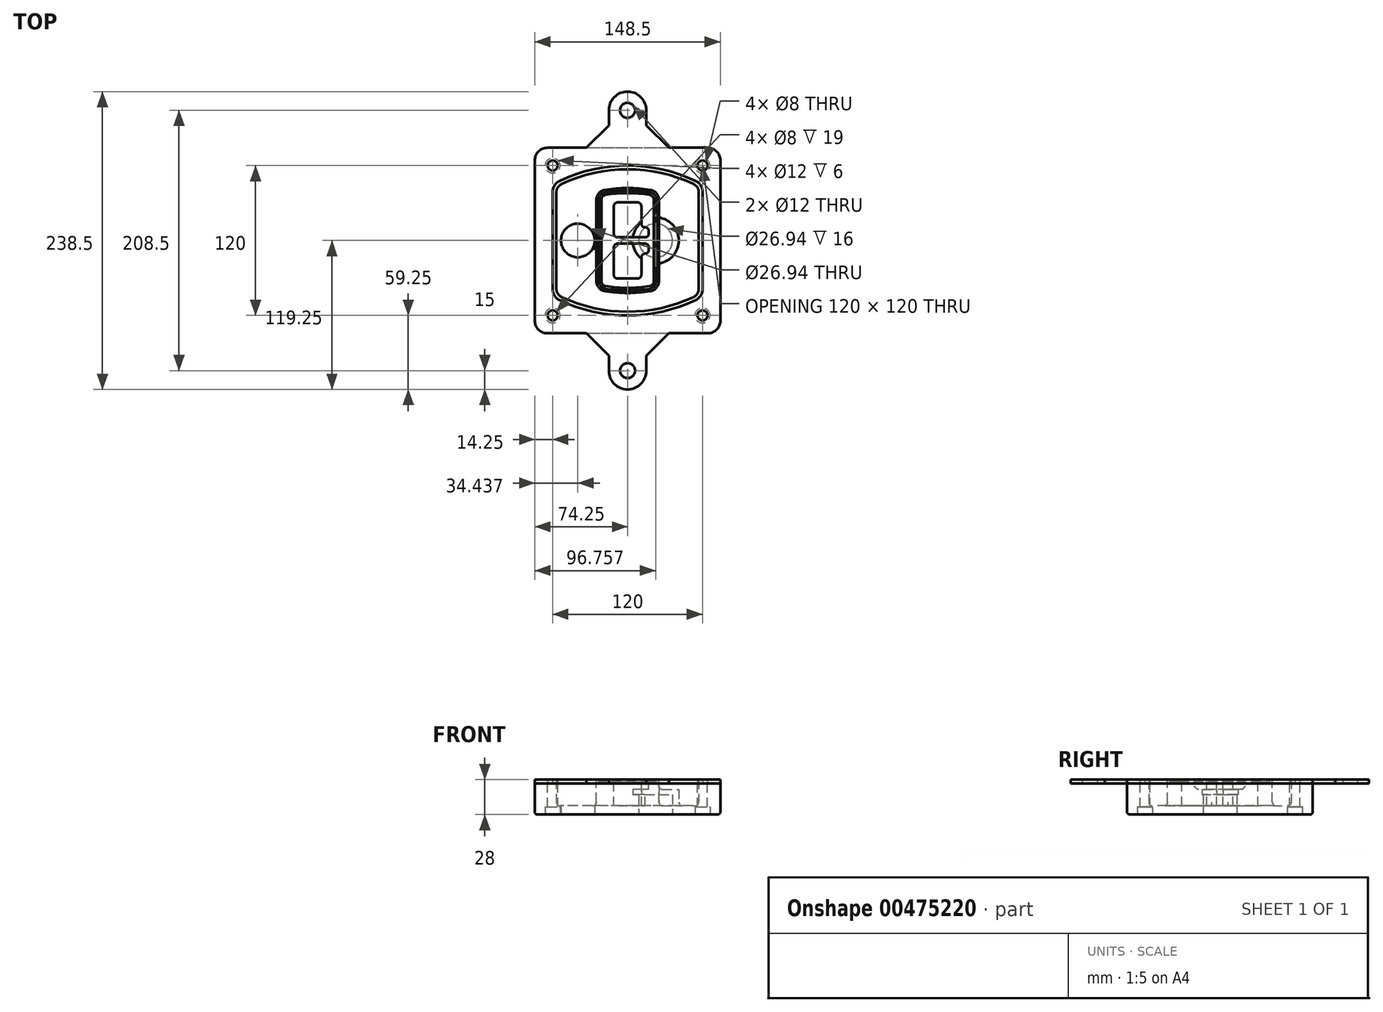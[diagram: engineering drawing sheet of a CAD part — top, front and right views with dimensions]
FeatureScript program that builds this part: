
annotation { "Feature Type Name" : "Feature", "Feature Type Description" : "" }
export const myFeature = defineFeature(function(context is Context, id is Id, definition is map)
    precondition{}
    {
        {
            var Q0;
            Q0=qCreatedBy(makeId("Top.planeOp"),FACE);
            var sketch = newSketch(context, id + "F0", { "sketchPlane" : qUnion([Q0])});
            skPoint(sketch, "E0.rect.middle", {"position": v(0, 0) * mm});
            skLineSegment(sketch, "E1.bottom", {"start": v(-64.25, -74.25) * mm, "end": v(64.25, -74.25) * mm});
            skLineSegment(sketch, "E1.top", {"start": v(-64.25, 74.25) * mm, "end": v(64.25, 74.25) * mm});
            skLineSegment(sketch, "E1.left", {"start": v(-74.25, -64.25) * mm, "end": v(-74.25, 64.25) * mm});
            skLineSegment(sketch, "E1.right", {"start": v(74.25, -64.25) * mm, "end": v(74.25, 64.25) * mm});
            skLineSegment(sketch, "E2", {"start": v(-74.25, 74.25) * mm, "end": v(74.25, -74.25) * mm, "construction": true});
            skLineSegment(sketch, "E3", {"start": v(74.25, 74.25) * mm, "end": v(-74.25, -74.25) * mm, "construction": true});
            skCircle(sketch, "E4", {"center": v(-60, 60) * mm, "radius": 4 * mm});
            skCircle(sketch, "E5", {"center": v(60, 60) * mm, "radius": 4 * mm});
            skCircle(sketch, "E6", {"center": v(60, -60) * mm, "radius": 4 * mm});
            skCircle(sketch, "E7", {"center": v(-60, -60) * mm, "radius": 4 * mm});
            skLineSegment(sketch, "E8", {"start": v(-60, 60) * mm, "end": v(60, 60) * mm, "construction": true});
            skLineSegment(sketch, "E9", {"start": v(60, 60) * mm, "end": v(60, -60) * mm, "construction": true});
            skLineSegment(sketch, "E10", {"start": v(60, -60) * mm, "end": v(-60, -60) * mm, "construction": true});
            skLineSegment(sketch, "E11", {"start": v(-60, -60) * mm, "end": v(-60, 60) * mm, "construction": true});
            skLineSegment(sketch, "E12", {"start": v(-60, 38.83) * mm, "end": v(-60, -38.83) * mm});
            skLineSegment(sketch, "E13", {"start": v(60, 38.83) * mm, "end": v(60, -38.83) * mm});
            skArc(sketch, "E14", {"start": v(54.26, 47.88) * mm, "mid": v(0, 60) * mm, "end": v(-54.26, 47.88) * mm});
            skArc(sketch, "E15", {"start": v(-54.26, -47.88) * mm, "mid": v(0, -60) * mm, "end": v(54.26, -47.88) * mm});
            skLineSegment(sketch, "E16", {"start": v(-60, 0) * mm, "end": v(60, 0) * mm, "construction": true});
            skPoint(sketch, "E17.visualSharp", {"position": v(-60, -45) * mm});
            skArc(sketch, "E17.filletArc", {"start": v(-60, -38.83) * mm, "mid": v(-58.44, -44.2) * mm, "end": v(-54.26, -47.88) * mm});
            skPoint(sketch, "E18.visualSharp", {"position": v(-60, 45) * mm});
            skArc(sketch, "E18.filletArc", {"start": v(-54.26, 47.88) * mm, "mid": v(-58.44, 44.2) * mm, "end": v(-60, 38.83) * mm});
            skPoint(sketch, "E19.visualSharp", {"position": v(60, 45) * mm});
            skArc(sketch, "E19.filletArc", {"start": v(60, 38.83) * mm, "mid": v(58.44, 44.2) * mm, "end": v(54.26, 47.88) * mm});
            skPoint(sketch, "E20.visualSharp", {"position": v(60, -45) * mm});
            skArc(sketch, "E20.filletArc", {"start": v(54.26, -47.88) * mm, "mid": v(58.44, -44.2) * mm, "end": v(60, -38.83) * mm});
            skPoint(sketch, "E21.visualSharp", {"position": v(-74.25, 74.25) * mm});
            skArc(sketch, "E21.filletArc", {"start": v(-64.25, 74.25) * mm, "mid": v(-71.32, 71.32) * mm, "end": v(-74.25, 64.25) * mm});
            skPoint(sketch, "E22.visualSharp", {"position": v(74.25, 74.25) * mm});
            skArc(sketch, "E22.filletArc", {"start": v(74.25, 64.25) * mm, "mid": v(71.32, 71.32) * mm, "end": v(64.25, 74.25) * mm});
            skPoint(sketch, "E23.visualSharp", {"position": v(74.25, -74.25) * mm});
            skArc(sketch, "E23.filletArc", {"start": v(64.25, -74.25) * mm, "mid": v(71.32, -71.32) * mm, "end": v(74.25, -64.25) * mm});
            skPoint(sketch, "E24.visualSharp", {"position": v(-74.25, -74.25) * mm});
            skArc(sketch, "E24.filletArc", {"start": v(-74.25, -64.25) * mm, "mid": v(-71.32, -71.32) * mm, "end": v(-64.25, -74.25) * mm});
            skArc(sketch, "E25.0", {"start": v(57, 38.83) * mm, "mid": v(55.9, 42.58) * mm, "end": v(52.98, 45.17) * mm});
            skLineSegment(sketch, "E25.1", {"start": v(57, 38.83) * mm, "end": v(57, -38.83) * mm});
            skArc(sketch, "E25.2", {"start": v(52.98, -45.17) * mm, "mid": v(55.9, -42.58) * mm, "end": v(57, -38.83) * mm});
            skArc(sketch, "E25.3", {"start": v(-52.98, -45.17) * mm, "mid": v(0, -57) * mm, "end": v(52.98, -45.17) * mm});
            skArc(sketch, "E25.4", {"start": v(-57, -38.83) * mm, "mid": v(-55.9, -42.58) * mm, "end": v(-52.98, -45.17) * mm});
            skArc(sketch, "E25.5", {"start": v(52.98, 45.17) * mm, "mid": v(0, 57) * mm, "end": v(-52.98, 45.17) * mm});
            skLineSegment(sketch, "E25.6", {"start": v(-57, 38.83) * mm, "end": v(-57, -38.83) * mm});
            skArc(sketch, "E25.7", {"start": v(-52.98, 45.17) * mm, "mid": v(-55.9, 42.58) * mm, "end": v(-57, 38.83) * mm});
            skArc(sketch, "E26.0", {"start": v(-55.96, 51.5) * mm, "mid": v(-61.82, 46.33) * mm, "end": v(-64, 38.83) * mm});
            skArc(sketch, "E26.1", {"start": v(55.96, 51.5) * mm, "mid": v(0, 64) * mm, "end": v(-55.96, 51.5) * mm});
            skArc(sketch, "E26.2", {"start": v(64, 38.83) * mm, "mid": v(61.82, 46.33) * mm, "end": v(55.96, 51.5) * mm});
            skLineSegment(sketch, "E26.3", {"start": v(64, 38.83) * mm, "end": v(64, -38.83) * mm});
            skArc(sketch, "E26.4", {"start": v(55.96, -51.5) * mm, "mid": v(61.82, -46.33) * mm, "end": v(64, -38.83) * mm});
            skLineSegment(sketch, "E26.5", {"start": v(-64, 38.83) * mm, "end": v(-64, -38.83) * mm});
            skArc(sketch, "E26.6", {"start": v(-55.96, -51.5) * mm, "mid": v(0, -64) * mm, "end": v(55.96, -51.5) * mm});
            skArc(sketch, "E26.7", {"start": v(-64, -38.83) * mm, "mid": v(-61.82, -46.33) * mm, "end": v(-55.96, -51.5) * mm});
            skSolve(sketch);
        }
        {
            var Q0;
            Q0=makeQuery(id+"F0.imprint","IMPRINT",FACE,{"disambiguationData":[TD([[makeQuery(id+"F0.imprint","IMPRINT",EDGE,{"derivedFrom":sQuery(id+"F0.wireOp",EDGE,"E1.bottom")}),1.0]])]});
            var Q1;
            Q1=makeQuery(id+"F0.imprint","IMPRINT",FACE,{"disambiguationData":[TD([[makeQuery(id+"F0.imprint","IMPRINT",EDGE,{"derivedFrom":sQuery(id+"F0.wireOp",EDGE,"E12")}),1.0]])]});
            var Q2;
            Q2=makeQuery(id+"F0.imprint","IMPRINT",FACE,{"disambiguationData":[TD([[makeQuery(id+"F0.imprint","IMPRINT",EDGE,{"derivedFrom":sQuery(id+"F0.wireOp",EDGE,"E25.0")}),1.0]])]});
            var Q3;
            Q3=makeQuery(id+"F0.imprint","IMPRINT",FACE,{"disambiguationData":[TD([[makeQuery(id+"F0.imprint","IMPRINT",EDGE,{"derivedFrom":sQuery(id+"F0.wireOp",EDGE,"E12")}),-1.0]])]});
            extrude(context, id + "F1", {"entities" : qUnion([Q0, Q1, Q2, Q3]), "oppositeDirection" : true, "depth" : 25 * mm});
        }
        {
            var Q0;
            Q0=makeQuery(id+"F0.imprint","IMPRINT",FACE,{"disambiguationData":[TD([[makeQuery(id+"F0.imprint","IMPRINT",EDGE,{"derivedFrom":sQuery(id+"F0.wireOp",EDGE,"E12")}),1.0]])]});
            extrude(context, id + "F2", {"entities" : qUnion([Q0]), "operationType" : NewBodyOperationType.ADD, "depth" : 3 * mm});
        }
        {
            var Q0;
            Q0=makeQuery(id+"F0.imprint","IMPRINT",FACE,{"disambiguationData":[TD([[makeQuery(id+"F0.imprint","IMPRINT",EDGE,{"derivedFrom":sQuery(id+"F0.wireOp",EDGE,"E25.0")}),1.0]])]});
            extrude(context, id + "F3", {"entities" : qUnion([Q0]), "operationType" : NewBodyOperationType.REMOVE, "oppositeDirection" : true, "depth" : 18 * mm});
        }
        {
            var Q0;
            Q0=makeQuery(id+"F2.opExtrude","CAP_FACE",FACE,{"disambiguationData":[OSD([sQuery(id+"F0.wireOp",EDGE,"E12"),sQuery(id+"F0.wireOp",EDGE,"E13"),sQuery(id+"F0.wireOp",EDGE,"E14"),sQuery(id+"F0.wireOp",EDGE,"E15"),sQuery(id+"F0.wireOp",EDGE,"E17.filletArc"),sQuery(id+"F0.wireOp",EDGE,"E18.filletArc"),sQuery(id+"F0.wireOp",EDGE,"E19.filletArc"),sQuery(id+"F0.wireOp",EDGE,"E20.filletArc"),sQuery(id+"F0.wireOp",EDGE,"E25.0"),sQuery(id+"F0.wireOp",EDGE,"E25.1"),sQuery(id+"F0.wireOp",EDGE,"E25.2"),sQuery(id+"F0.wireOp",EDGE,"E25.3"),sQuery(id+"F0.wireOp",EDGE,"E25.4"),sQuery(id+"F0.wireOp",EDGE,"E25.5"),sQuery(id+"F0.wireOp",EDGE,"E25.6"),sQuery(id+"F0.wireOp",EDGE,"E25.7")])],"isStart":false});
            var sketch = newSketch(context, id + "F4", { "sketchPlane" : qUnion([Q0])});
            skArc(sketch, "E27.0", {"start": v(-18.34, -40.45) * mm, "mid": v(0, -42) * mm, "end": v(18.34, -40.45) * mm});
            skArc(sketch, "E28.0", {"start": v(18.34, 40.45) * mm, "mid": v(0, 42) * mm, "end": v(-18.34, 40.45) * mm});
            skLineSegment(sketch, "E29", {"start": v(-25, 32.57) * mm, "end": v(-25, -32.57) * mm});
            skLineSegment(sketch, "E30", {"start": v(25, 32.57) * mm, "end": v(25, -32.57) * mm});
            skLineSegment(sketch, "E31", {"start": v(-25, 39.1) * mm, "end": v(25, 39.1) * mm, "construction": true});
            skLineSegment(sketch, "E32", {"start": v(-25, -39.1) * mm, "end": v(25, -39.1) * mm, "construction": true});
            skPoint(sketch, "E33.visualSharp", {"position": v(-25, 39.1) * mm});
            skArc(sketch, "E33.filletArc", {"start": v(-18.34, 40.45) * mm, "mid": v(-23.11, 37.73) * mm, "end": v(-25, 32.57) * mm});
            skPoint(sketch, "E34.visualSharp", {"position": v(25, 39.1) * mm});
            skArc(sketch, "E34.filletArc", {"start": v(25, 32.57) * mm, "mid": v(23.11, 37.73) * mm, "end": v(18.34, 40.45) * mm});
            skPoint(sketch, "E35.visualSharp", {"position": v(25, -39.1) * mm});
            skArc(sketch, "E35.filletArc", {"start": v(18.34, -40.45) * mm, "mid": v(23.11, -37.73) * mm, "end": v(25, -32.57) * mm});
            skPoint(sketch, "E36.visualSharp", {"position": v(-25, -39.1) * mm});
            skArc(sketch, "E36.filletArc", {"start": v(-25, -32.57) * mm, "mid": v(-23.11, -37.73) * mm, "end": v(-18.34, -40.45) * mm});
            skArc(sketch, "E37.0", {"start": v(52.98, 45.17) * mm, "mid": v(0, 57) * mm, "end": v(-52.98, 45.17) * mm});
            skArc(sketch, "E37.1", {"start": v(-52.98, 45.17) * mm, "mid": v(-55.9, 42.58) * mm, "end": v(-57, 38.83) * mm});
            skLineSegment(sketch, "E37.2", {"start": v(-57, 38.83) * mm, "end": v(-57, -38.83) * mm});
            skArc(sketch, "E37.3", {"start": v(-57, -38.83) * mm, "mid": v(-55.9, -42.58) * mm, "end": v(-52.98, -45.17) * mm});
            skArc(sketch, "E37.4", {"start": v(-52.98, -45.17) * mm, "mid": v(0, -57) * mm, "end": v(52.98, -45.17) * mm});
            skArc(sketch, "E37.5", {"start": v(52.98, -45.17) * mm, "mid": v(55.9, -42.58) * mm, "end": v(57, -38.83) * mm});
            skLineSegment(sketch, "E37.6", {"start": v(57, 38.83) * mm, "end": v(57, -38.83) * mm});
            skArc(sketch, "E37.7", {"start": v(57, 38.83) * mm, "mid": v(55.9, 42.58) * mm, "end": v(52.98, 45.17) * mm});
            skLineSegment(sketch, "E38.0", {"start": v(23, 32.57) * mm, "end": v(23, -32.57) * mm});
            skArc(sketch, "E38.1", {"start": v(18, -38.48) * mm, "mid": v(21.58, -36.44) * mm, "end": v(23, -32.57) * mm});
            skArc(sketch, "E38.2", {"start": v(-18, -38.48) * mm, "mid": v(0, -40) * mm, "end": v(18, -38.48) * mm});
            skArc(sketch, "E38.3", {"start": v(-23, -32.57) * mm, "mid": v(-21.58, -36.44) * mm, "end": v(-18, -38.48) * mm});
            skLineSegment(sketch, "E38.4", {"start": v(-23, 32.57) * mm, "end": v(-23, -32.57) * mm});
            skArc(sketch, "E38.5", {"start": v(23, 32.57) * mm, "mid": v(21.58, 36.44) * mm, "end": v(18, 38.48) * mm});
            skArc(sketch, "E38.6", {"start": v(-18, 38.48) * mm, "mid": v(-21.58, 36.44) * mm, "end": v(-23, 32.57) * mm});
            skArc(sketch, "E38.7", {"start": v(18, 38.48) * mm, "mid": v(0, 40) * mm, "end": v(-18, 38.48) * mm});
            skArc(sketch, "E39.0", {"start": v(21, 32.57) * mm, "mid": v(20.06, 35.15) * mm, "end": v(17.67, 36.5) * mm});
            skLineSegment(sketch, "E39.1", {"start": v(21, 32.57) * mm, "end": v(21, -32.57) * mm});
            skArc(sketch, "E39.2", {"start": v(17.67, -36.5) * mm, "mid": v(20.06, -35.15) * mm, "end": v(21, -32.57) * mm});
            skArc(sketch, "E39.3", {"start": v(-17.67, -36.5) * mm, "mid": v(0, -38) * mm, "end": v(17.67, -36.5) * mm});
            skArc(sketch, "E39.4", {"start": v(-21, -32.57) * mm, "mid": v(-20.06, -35.15) * mm, "end": v(-17.67, -36.5) * mm});
            skArc(sketch, "E39.5", {"start": v(17.67, 36.5) * mm, "mid": v(0, 38) * mm, "end": v(-17.67, 36.5) * mm});
            skLineSegment(sketch, "E39.6", {"start": v(-21, 32.57) * mm, "end": v(-21, -32.57) * mm});
            skArc(sketch, "E39.7", {"start": v(-17.67, 36.5) * mm, "mid": v(-20.06, 35.15) * mm, "end": v(-21, 32.57) * mm});
            skLineSegment(sketch, "E40", {"start": v(-25, 0) * mm, "end": v(25, 0) * mm, "construction": true});
            skLineSegment(sketch, "E41", {"start": v(-11, 5.5) * mm, "end": v(-11, 27.5) * mm});
            skLineSegment(sketch, "E42", {"start": v(-8, 30.5) * mm, "end": v(8, 30.5) * mm});
            skLineSegment(sketch, "E43", {"start": v(11, 27.5) * mm, "end": v(11, 13.5) * mm});
            skLineSegment(sketch, "E44", {"start": v(14, 10.5) * mm, "end": v(14, 10.5) * mm});
            skLineSegment(sketch, "E45", {"start": v(17, 7.5) * mm, "end": v(17, 5.5) * mm});
            skLineSegment(sketch, "E46", {"start": v(14, 2.5) * mm, "end": v(-8, 2.5) * mm});
            skPoint(sketch, "E47.visualSharp", {"position": v(-11, 30.5) * mm});
            skArc(sketch, "E47.filletArc", {"start": v(-8, 30.5) * mm, "mid": v(-10.12, 29.62) * mm, "end": v(-11, 27.5) * mm});
            skPoint(sketch, "E48.visualSharp", {"position": v(11, 30.5) * mm});
            skArc(sketch, "E48.filletArc", {"start": v(11, 27.5) * mm, "mid": v(10.12, 29.62) * mm, "end": v(8, 30.5) * mm});
            skPoint(sketch, "E49.visualSharp", {"position": v(11, 10.5) * mm});
            skArc(sketch, "E49.filletArc", {"start": v(11, 13.5) * mm, "mid": v(11.88, 11.38) * mm, "end": v(14, 10.5) * mm});
            skPoint(sketch, "E50.visualSharp", {"position": v(17, 10.5) * mm});
            skArc(sketch, "E50.filletArc", {"start": v(17, 7.5) * mm, "mid": v(16.12, 9.62) * mm, "end": v(14, 10.5) * mm});
            skPoint(sketch, "E51.visualSharp", {"position": v(17, 2.5) * mm});
            skArc(sketch, "E51.filletArc", {"start": v(14, 2.5) * mm, "mid": v(16.12, 3.38) * mm, "end": v(17, 5.5) * mm});
            skPoint(sketch, "E52.visualSharp", {"position": v(-11, 2.5) * mm});
            skArc(sketch, "E52.filletArc", {"start": v(-11, 5.5) * mm, "mid": v(-10.12, 3.38) * mm, "end": v(-8, 2.5) * mm});
            skLineSegment(sketch, "E53.0.MirrorCS", {"start": v(14, -2.5) * mm, "end": v(-8, -2.5) * mm});
            skArc(sketch, "E54.0.MirrorCS", {"start": v(-11, -5.5) * mm, "mid": v(-10.12, -3.38) * mm, "end": v(-8, -2.5) * mm});
            skLineSegment(sketch, "E55.0.MirrorCS", {"start": v(-11, -5.5) * mm, "end": v(-11, -27.5) * mm});
            skArc(sketch, "E56.0.MirrorCS", {"start": v(-8, -30.5) * mm, "mid": v(-10.12, -29.62) * mm, "end": v(-11, -27.5) * mm});
            skLineSegment(sketch, "E57.0.MirrorCS", {"start": v(-8, -30.5) * mm, "end": v(8, -30.5) * mm});
            skArc(sketch, "E58.0.MirrorCS", {"start": v(11, -27.5) * mm, "mid": v(10.12, -29.62) * mm, "end": v(8, -30.5) * mm});
            skLineSegment(sketch, "E59.0.MirrorCS", {"start": v(11, -27.5) * mm, "end": v(11, -13.5) * mm});
            skArc(sketch, "E60.0.MirrorCS", {"start": v(11, -13.5) * mm, "mid": v(11.88, -11.38) * mm, "end": v(14, -10.5) * mm});
            skArc(sketch, "E61.0.MirrorCS", {"start": v(17, -7.5) * mm, "mid": v(16.12, -9.62) * mm, "end": v(14, -10.5) * mm});
            skLineSegment(sketch, "E62.0.MirrorCS", {"start": v(17, -7.5) * mm, "end": v(17, -5.5) * mm});
            skArc(sketch, "E63.0.MirrorCS", {"start": v(14, -2.5) * mm, "mid": v(16.12, -3.38) * mm, "end": v(17, -5.5) * mm});
            skSolve(sketch);
        }
        {
            var Q0;
            Q0=makeQuery(id+"F4.imprint","IMPRINT",FACE,{"disambiguationData":[TD([[makeQuery(id+"F4.imprint","IMPRINT",EDGE,{"derivedFrom":sQuery(id+"F4.wireOp",EDGE,"E27.0")}),1.0]])]});
            var Q1;
            Q1=makeQuery(id+"F4.imprint","IMPRINT",FACE,{"disambiguationData":[TD([[makeQuery(id+"F4.imprint","IMPRINT",EDGE,{"derivedFrom":sQuery(id+"F4.wireOp",EDGE,"E38.0")}),-1.0]])]});
            var Q2;
            Q2=makeQuery(id+"F4.imprint","IMPRINT",FACE,{"disambiguationData":[TD([[makeQuery(id+"F4.imprint","IMPRINT",EDGE,{"derivedFrom":sQuery(id+"F4.wireOp",EDGE,"E39.0")}),1.0]])]});
            extrude(context, id + "F5", {"entities" : qUnion([Q0, Q1, Q2]), "operationType" : NewBodyOperationType.ADD, "endBound" : BoundingType.UP_TO_NEXT, "oppositeDirection" : true, "depth" : 25 * mm});
        }
        {
            var Q0;
            Q0=makeQuery(id+"F4.imprint","IMPRINT",FACE,{"disambiguationData":[TD([[makeQuery(id+"F4.imprint","IMPRINT",EDGE,{"derivedFrom":sQuery(id+"F4.wireOp",EDGE,"E38.0")}),-1.0]])]});
            extrude(context, id + "F6", {"entities" : qUnion([Q0]), "operationType" : NewBodyOperationType.REMOVE, "oppositeDirection" : true, "depth" : 2 * mm});
        }
        {
            var Q0;
            Q0=makeQuery(id+"F1.opExtrude","CAP_FACE",FACE,{"disambiguationData":[OSD([sQuery(id+"F0.wireOp",EDGE,"E1.bottom"),sQuery(id+"F0.wireOp",EDGE,"E1.top"),sQuery(id+"F0.wireOp",EDGE,"E1.left"),sQuery(id+"F0.wireOp",EDGE,"E1.right"),sQuery(id+"F0.wireOp",EDGE,"E4"),sQuery(id+"F0.wireOp",EDGE,"E5"),sQuery(id+"F0.wireOp",EDGE,"E6"),sQuery(id+"F0.wireOp",EDGE,"E7"),sQuery(id+"F0.wireOp",EDGE,"E21.filletArc"),sQuery(id+"F0.wireOp",EDGE,"E22.filletArc"),sQuery(id+"F0.wireOp",EDGE,"E23.filletArc"),sQuery(id+"F0.wireOp",EDGE,"E24.filletArc")])],"isStart":false});
            var sketch = newSketch(context, id + "F7", { "sketchPlane" : qUnion([Q0])});
            skCircle(sketch, "E64", {"center": v(22.5, 0) * mm, "radius": 13.47 * mm});
            skCircle(sketch, "E65", {"center": v(-39.81, 0) * mm, "radius": 13.47 * mm});
            skLineSegment(sketch, "E66", {"start": v(74.25, 0) * mm, "end": v(-74.25, 0) * mm});
            skCircle(sketch, "E67", {"center": v(22.5, 0) * mm, "radius": 18.47 * mm});
            skCircle(sketch, "E68", {"center": v(60, -60) * mm, "radius": 6 * mm});
            skCircle(sketch, "E69", {"center": v(-60, -60) * mm, "radius": 6 * mm});
            skCircle(sketch, "E70", {"center": v(-60, 60) * mm, "radius": 6 * mm});
            skCircle(sketch, "E71", {"center": v(60, 60) * mm, "radius": 6 * mm});
            skSolve(sketch);
        }
        {
            var Q0;
            {var subQ1=sQuery(id+"F7.wireOp",EDGE,"E66");var subQ4=sQuery(id+"F7.wireOp",EDGE,"E64");var subQ6=makeQuery(id+"F7.imprint","INTERSECT",VERTEX,{"disambiguationData":[OD(0.0)],"derivedFrom":[subQ4,subQ1]});Q0=makeQuery(id+"F7.imprint","IMPRINT",FACE,{"disambiguationData":[TD([[makeQuery(id+"F7.imprint","IMPRINT",EDGE,{"disambiguationData":[TD([[subQ6,-1.0]])],"derivedFrom":subQ4}),-1.0]])]});}
            var Q1;
            {var subQ0=sQuery(id+"F7.wireOp",EDGE,"E66");var subQ1=sQuery(id+"F7.wireOp",EDGE,"E64");var subQ3=makeQuery(id+"F7.imprint","INTERSECT",VERTEX,{"disambiguationData":[OD(0.0)],"derivedFrom":[subQ1,subQ0]});Q1=makeQuery(id+"F7.imprint","IMPRINT",FACE,{"disambiguationData":[TD([[makeQuery(id+"F7.imprint","IMPRINT",EDGE,{"disambiguationData":[TD([[subQ3,-1.0]])],"derivedFrom":subQ1}),1.0]])]});}
            var Q2;
            {var subQ0=sQuery(id+"F7.wireOp",EDGE,"E66");var subQ1=sQuery(id+"F7.wireOp",EDGE,"E64");var subQ3=makeQuery(id+"F7.imprint","INTERSECT",VERTEX,{"disambiguationData":[OD(0.0)],"derivedFrom":[subQ1,subQ0]});Q2=makeQuery(id+"F7.imprint","IMPRINT",FACE,{"disambiguationData":[TD([[makeQuery(id+"F7.imprint","IMPRINT",EDGE,{"disambiguationData":[TD([[subQ3,1.0]])],"derivedFrom":subQ1}),1.0]])]});}
            var Q3;
            {var subQ1=sQuery(id+"F7.wireOp",EDGE,"E66");var subQ4=sQuery(id+"F7.wireOp",EDGE,"E64");var subQ6=makeQuery(id+"F7.imprint","INTERSECT",VERTEX,{"disambiguationData":[OD(0.0)],"derivedFrom":[subQ4,subQ1]});Q3=makeQuery(id+"F7.imprint","IMPRINT",FACE,{"disambiguationData":[TD([[makeQuery(id+"F7.imprint","IMPRINT",EDGE,{"disambiguationData":[TD([[subQ6,1.0]])],"derivedFrom":subQ4}),-1.0]])]});}
            extrude(context, id + "F8", {"entities" : qUnion([Q0, Q1, Q2, Q3]), "operationType" : NewBodyOperationType.ADD, "oppositeDirection" : true, "depth" : 20 * mm});
        }
        {
            var Q0;
            {var subQ0=sQuery(id+"F7.wireOp",EDGE,"E66");var subQ1=sQuery(id+"F7.wireOp",EDGE,"E64");var subQ3=makeQuery(id+"F7.imprint","INTERSECT",VERTEX,{"disambiguationData":[OD(0.0)],"derivedFrom":[subQ1,subQ0]});Q0=makeQuery(id+"F7.imprint","IMPRINT",FACE,{"disambiguationData":[TD([[makeQuery(id+"F7.imprint","IMPRINT",EDGE,{"disambiguationData":[TD([[subQ3,-1.0]])],"derivedFrom":subQ1}),1.0]])]});}
            var Q1;
            {var subQ0=sQuery(id+"F7.wireOp",EDGE,"E66");var subQ1=sQuery(id+"F7.wireOp",EDGE,"E64");var subQ3=makeQuery(id+"F7.imprint","INTERSECT",VERTEX,{"disambiguationData":[OD(0.0)],"derivedFrom":[subQ1,subQ0]});Q1=makeQuery(id+"F7.imprint","IMPRINT",FACE,{"disambiguationData":[TD([[makeQuery(id+"F7.imprint","IMPRINT",EDGE,{"disambiguationData":[TD([[subQ3,1.0]])],"derivedFrom":subQ1}),1.0]])]});}
            extrude(context, id + "F9", {"entities" : qUnion([Q0, Q1]), "operationType" : NewBodyOperationType.REMOVE, "oppositeDirection" : true, "depth" : 16 * mm});
        }
        {
            var Q0;
            {var subQ0=sQuery(id+"F7.wireOp",EDGE,"E66");var subQ1=sQuery(id+"F7.wireOp",EDGE,"E65");var subQ3=makeQuery(id+"F7.imprint","INTERSECT",VERTEX,{"disambiguationData":[OD(0.0)],"derivedFrom":[subQ1,subQ0]});Q0=makeQuery(id+"F7.imprint","IMPRINT",FACE,{"disambiguationData":[TD([[makeQuery(id+"F7.imprint","IMPRINT",EDGE,{"disambiguationData":[TD([[subQ3,-1.0]])],"derivedFrom":subQ1}),1.0]])]});}
            var Q1;
            {var subQ0=sQuery(id+"F7.wireOp",EDGE,"E66");var subQ1=sQuery(id+"F7.wireOp",EDGE,"E65");var subQ3=makeQuery(id+"F7.imprint","INTERSECT",VERTEX,{"disambiguationData":[OD(0.0)],"derivedFrom":[subQ1,subQ0]});Q1=makeQuery(id+"F7.imprint","IMPRINT",FACE,{"disambiguationData":[TD([[makeQuery(id+"F7.imprint","IMPRINT",EDGE,{"disambiguationData":[TD([[subQ3,1.0]])],"derivedFrom":subQ1}),1.0]])]});}
            extrude(context, id + "F10", {"entities" : qUnion([Q0, Q1]), "operationType" : NewBodyOperationType.REMOVE, "oppositeDirection" : true, "depth" : 25 * mm});
        }
        {
            var Q0;
            Q0=makeQuery(id+"F7.imprint","IMPRINT",FACE,{"disambiguationData":[TD([[makeQuery(id+"F7.imprint","IMPRINT",EDGE,{"derivedFrom":sQuery(id+"F7.wireOp",EDGE,"E68")}),1.0]])]});
            var Q1;
            Q1=makeQuery(id+"F7.imprint","IMPRINT",FACE,{"disambiguationData":[TD([[makeQuery(id+"F7.imprint","IMPRINT",EDGE,{"derivedFrom":makeQuery(id+"F1.opExtrude","CAP_EDGE",EDGE,{"disambiguationData":[OSD([sQuery(id+"F0.wireOp",EDGE,"E5")])],"isStart":false})}),-1.0]])]});
            var Q2;
            Q2=makeQuery(id+"F7.imprint","IMPRINT",FACE,{"disambiguationData":[TD([[makeQuery(id+"F7.imprint","IMPRINT",EDGE,{"derivedFrom":sQuery(id+"F7.wireOp",EDGE,"E69")}),1.0]])]});
            var Q3;
            Q3=makeQuery(id+"F7.imprint","IMPRINT",FACE,{"disambiguationData":[TD([[makeQuery(id+"F7.imprint","IMPRINT",EDGE,{"derivedFrom":makeQuery(id+"F1.opExtrude","CAP_EDGE",EDGE,{"disambiguationData":[OSD([sQuery(id+"F0.wireOp",EDGE,"E4")])],"isStart":false})}),-1.0]])]});
            var Q4;
            Q4=makeQuery(id+"F7.imprint","IMPRINT",FACE,{"disambiguationData":[TD([[makeQuery(id+"F7.imprint","IMPRINT",EDGE,{"derivedFrom":sQuery(id+"F7.wireOp",EDGE,"E70")}),1.0]])]});
            var Q5;
            Q5=makeQuery(id+"F7.imprint","IMPRINT",FACE,{"disambiguationData":[TD([[makeQuery(id+"F7.imprint","IMPRINT",EDGE,{"derivedFrom":makeQuery(id+"F1.opExtrude","CAP_EDGE",EDGE,{"disambiguationData":[OSD([sQuery(id+"F0.wireOp",EDGE,"E7")])],"isStart":false})}),-1.0]])]});
            var Q6;
            Q6=makeQuery(id+"F7.imprint","IMPRINT",FACE,{"disambiguationData":[TD([[makeQuery(id+"F7.imprint","IMPRINT",EDGE,{"derivedFrom":sQuery(id+"F7.wireOp",EDGE,"E71")}),1.0]])]});
            var Q7;
            Q7=makeQuery(id+"F7.imprint","IMPRINT",FACE,{"disambiguationData":[TD([[makeQuery(id+"F7.imprint","IMPRINT",EDGE,{"derivedFrom":makeQuery(id+"F1.opExtrude","CAP_EDGE",EDGE,{"disambiguationData":[OSD([sQuery(id+"F0.wireOp",EDGE,"E6")])],"isStart":false})}),-1.0]])]});
            extrude(context, id + "F11", {"entities" : qUnion([Q0, Q1, Q2, Q3, Q4, Q5, Q6, Q7]), "operationType" : NewBodyOperationType.REMOVE, "oppositeDirection" : true, "depth" : 6 * mm});
        }
        {
            var Q0;
            Q0=makeQuery(id+"F9.boolean.opBoolean","COPY",FACE,{"derivedFrom":makeQuery(id+"F9.opExtrude","CAP_FACE",FACE,{"disambiguationData":[OSD([sQuery(id+"F7.wireOp",EDGE,"E64")])],"isStart":false})});
            var sketch = newSketch(context, id + "F12", { "sketchPlane" : qUnion([Q0])});
            skArc(sketch, "E72.0", {"start": v(11, 14.45) * mm, "mid": v(6.45, 9.13) * mm, "end": v(4.2, 2.5) * mm});
            skArc(sketch, "E72.1", {"start": v(4.2, -2.5) * mm, "mid": v(6.45, -9.13) * mm, "end": v(11, -14.45) * mm});
            skLineSegment(sketch, "E73", {"start": v(4.2, -2.5) * mm, "end": v(14, -2.5) * mm});
            skLineSegment(sketch, "E74.0", {"start": v(14, 2.5) * mm, "end": v(4.2, 2.5) * mm});
            skArc(sketch, "E74.1", {"start": v(14, 2.5) * mm, "mid": v(16.12, 3.38) * mm, "end": v(17, 5.5) * mm});
            skLineSegment(sketch, "E74.2", {"start": v(17, 7.5) * mm, "end": v(17, 5.5) * mm});
            skArc(sketch, "E74.3", {"start": v(17, 7.5) * mm, "mid": v(16.12, 9.62) * mm, "end": v(14, 10.5) * mm});
            skArc(sketch, "E74.4", {"start": v(11, 13.5) * mm, "mid": v(11.88, 11.38) * mm, "end": v(14, 10.5) * mm});
            skLineSegment(sketch, "E74.5", {"start": v(11, 14.45) * mm, "end": v(11, 13.5) * mm});
            skLineSegment(sketch, "E74.7", {"start": v(14, -2.5) * mm, "end": v(4.2, -2.5) * mm});
            skArc(sketch, "E74.8", {"start": v(14, -2.5) * mm, "mid": v(16.12, -3.38) * mm, "end": v(17, -5.5) * mm});
            skLineSegment(sketch, "E74.9", {"start": v(17, -7.5) * mm, "end": v(17, -5.5) * mm});
            skArc(sketch, "E74.10", {"start": v(17, -7.5) * mm, "mid": v(16.12, -9.62) * mm, "end": v(14, -10.5) * mm});
            skArc(sketch, "E74.11", {"start": v(11, -13.5) * mm, "mid": v(11.88, -11.38) * mm, "end": v(14, -10.5) * mm});
            skLineSegment(sketch, "E74.12", {"start": v(11, -14.45) * mm, "end": v(11, -13.5) * mm});
            skPoint(sketch, "E75.orphan", {"position": v(11, -27.5) * mm});
            skPoint(sketch, "E76.orphan", {"position": v(-8, -2.5) * mm});
            skPoint(sketch, "E77.orphan", {"position": v(-8, 2.5) * mm});
            skPoint(sketch, "E78.orphan", {"position": v(11, 27.5) * mm});
            skSolve(sketch);
        }
        {
            var Q0;
            {var subQ7=sQuery(id+"F12.wireOp",EDGE,"E72.0");var subQ14=sQuery(id+"F12.wireOp",EDGE,"E72.1");var subQ16=sQuery(id+"F12.wireOp",EDGE,"E74.1");var subQ18=sQuery(id+"F12.wireOp",EDGE,"E74.8");Q0=qUnion([makeQuery(id+"F12.imprint","IMPRINT",FACE,{"disambiguationData":[TD([[makeQuery(id+"F12.imprint","IMPRINT",EDGE,{"derivedFrom":subQ7}),1.0]])]}),makeQuery(id+"F12.imprint","IMPRINT",FACE,{"disambiguationData":[TD([[makeQuery(id+"F12.imprint","IMPRINT",EDGE,{"derivedFrom":subQ14}),1.0]])]}),makeQuery(id+"F12.imprint","IMPRINT",FACE,{"disambiguationData":[TD([[makeQuery(id+"F12.imprint","IMPRINT",EDGE,{"derivedFrom":subQ16}),1.0]])]}),makeQuery(id+"F12.imprint","IMPRINT",FACE,{"disambiguationData":[TD([[makeQuery(id+"F12.imprint","IMPRINT",EDGE,{"derivedFrom":subQ18}),-1.0]])]})]);}
            var Q1;
            Q1=makeQuery(id+"F5.boolean.opBoolean","SPLIT",FACE,{"disambiguationData":[TD([makeQuery(id+"F5.opExtrude","SWEPT_FACE",FACE,{"disambiguationData":[OSD([sQuery(id+"F4.wireOp",EDGE,"E41")])]})])],"derivedFrom":makeQuery(id+"F3.boolean.opBoolean","COPY",FACE,{"derivedFrom":makeQuery(id+"F3.opExtrude","CAP_FACE",FACE,{"disambiguationData":[OSD([sQuery(id+"F0.wireOp",EDGE,"E25.0"),sQuery(id+"F0.wireOp",EDGE,"E25.1"),sQuery(id+"F0.wireOp",EDGE,"E25.2"),sQuery(id+"F0.wireOp",EDGE,"E25.3"),sQuery(id+"F0.wireOp",EDGE,"E25.4"),sQuery(id+"F0.wireOp",EDGE,"E25.5"),sQuery(id+"F0.wireOp",EDGE,"E25.6"),sQuery(id+"F0.wireOp",EDGE,"E25.7")])],"isStart":false})})});
            extrude(context, id + "F13", {"entities" : qUnion([Q0]), "operationType" : NewBodyOperationType.REMOVE, "endBound" : BoundingType.UP_TO_SURFACE, "endBoundEntityFace" : qUnion([Q1]), "depth" : 25 * mm});
        }
        {
            var Q0;
            Q0=makeQuery(id+"F3.boolean.opBoolean","COPY",EDGE,{"derivedFrom":makeQuery(id+"F3.opExtrude","CAP_EDGE",EDGE,{"disambiguationData":[OSD([sQuery(id+"F0.wireOp",EDGE,"E25.6")])],"isStart":false})});
            var Q1;
            Q1=makeQuery(id+"F8.boolean.opBoolean","INTERSECT",EDGE,{"derivedFrom":[makeQuery(id+"F5.opExtrude","SWEPT_FACE",FACE,{"disambiguationData":[OSD([sQuery(id+"F4.wireOp",EDGE,"E30")])]}),makeQuery(id+"F8.opExtrude","CAP_FACE",FACE,{"disambiguationData":[OSD([sQuery(id+"F7.wireOp",EDGE,"E67")])],"isStart":false})]});
            var Q2;
            Q2=makeQuery(id+"F8.boolean.opBoolean","INTERSECT",EDGE,{"disambiguationData":[OD(1.0)],"derivedFrom":[makeQuery(id+"F5.opExtrude","SWEPT_FACE",FACE,{"disambiguationData":[OSD([sQuery(id+"F4.wireOp",EDGE,"E30")])]}),makeQuery(id+"F8.opExtrude","SWEPT_FACE",FACE,{"disambiguationData":[OSD([sQuery(id+"F7.wireOp",EDGE,"E67")])]})]});
            var Q3;
            {var subQ0=sQuery(id+"F4.wireOp",EDGE,"E30");Q3=makeQuery(id+"F8.boolean.opBoolean","SPLIT",EDGE,{"disambiguationData":[TD([makeQuery(id+"F5.opExtrude","SWEPT_FACE",FACE,{"disambiguationData":[OSD([sQuery(id+"F4.wireOp",EDGE,"E35.filletArc")])]})])],"derivedFrom":makeQuery(id+"F5.opExtrude","CAP_EDGE",EDGE,{"disambiguationData":[OSD([subQ0])],"isStart":false})});}
            var Q4;
            {var subQ0=sQuery(id+"F0.wireOp",EDGE,"E25.7");var subQ1=sQuery(id+"F0.wireOp",EDGE,"E25.1");var subQ2=sQuery(id+"F0.wireOp",EDGE,"E25.6");var subQ3=sQuery(id+"F0.wireOp",EDGE,"E25.5");var subQ4=sQuery(id+"F0.wireOp",EDGE,"E25.4");var subQ5=sQuery(id+"F0.wireOp",EDGE,"E25.0");var subQ6=sQuery(id+"F0.wireOp",EDGE,"E25.2");var subQ7=sQuery(id+"F0.wireOp",EDGE,"E25.3");Q4=makeQuery(id+"F8.boolean.opBoolean","INTERSECT",EDGE,{"derivedFrom":[makeQuery(id+"F5.boolean.opBoolean","SPLIT",FACE,{"disambiguationData":[TD([makeQuery(id+"F2.opExtrude","SWEPT_FACE",FACE,{"disambiguationData":[OSD([subQ5])]})])],"derivedFrom":makeQuery(id+"F3.boolean.opBoolean","COPY",FACE,{"derivedFrom":makeQuery(id+"F3.opExtrude","CAP_FACE",FACE,{"disambiguationData":[OSD([subQ5,subQ1,subQ6,subQ7,subQ4,subQ3,subQ2,subQ0])],"isStart":false})})}),makeQuery(id+"F8.opExtrude","SWEPT_FACE",FACE,{"disambiguationData":[OSD([sQuery(id+"F7.wireOp",EDGE,"E67")])]})]});}
            var Q5;
            Q5=makeQuery(id+"F8.boolean.opBoolean","INTERSECT",EDGE,{"disambiguationData":[OD(0.0)],"derivedFrom":[makeQuery(id+"F5.opExtrude","SWEPT_FACE",FACE,{"disambiguationData":[OSD([sQuery(id+"F4.wireOp",EDGE,"E30")])]}),makeQuery(id+"F8.opExtrude","SWEPT_FACE",FACE,{"disambiguationData":[OSD([sQuery(id+"F7.wireOp",EDGE,"E67")])]})]});
            fillet(context, id + "F14", {"entities" : qUnion([Q0, Q1, Q2, Q3, Q4, Q5]), "radius" : 3 * mm, "tangentPropagation" : true, "allowEdgeOverflow" : false});
        }
        {
            var Q0;
            Q0=makeQuery(id+"F1.opExtrude","CAP_EDGE",EDGE,{"disambiguationData":[OSD([sQuery(id+"F0.wireOp",EDGE,"E1.bottom")])],"isStart":false});
            fillet(context, id + "F15", {"entities" : qUnion([Q0]), "radius" : 2 * mm, "tangentPropagation" : true, "allowEdgeOverflow" : false});
        }
        {
            var Q0;
            {var subQ0=sQuery(id+"F0.wireOp",EDGE,"E21.filletArc");var subQ1=sQuery(id+"F0.wireOp",EDGE,"E7");var subQ2=sQuery(id+"F0.wireOp",EDGE,"E6");var subQ3=sQuery(id+"F0.wireOp",EDGE,"E5");var subQ4=sQuery(id+"F0.wireOp",EDGE,"E4");var subQ5=sQuery(id+"F0.wireOp",EDGE,"E22.filletArc");var subQ6=sQuery(id+"F0.wireOp",EDGE,"E1.bottom");var subQ7=sQuery(id+"F0.wireOp",EDGE,"E1.right");var subQ8=sQuery(id+"F0.wireOp",EDGE,"E1.top");var subQ9=sQuery(id+"F0.wireOp",EDGE,"E1.left");var subQ10=sQuery(id+"F0.wireOp",EDGE,"E23.filletArc");var subQ11=sQuery(id+"F0.wireOp",EDGE,"E24.filletArc");Q0=makeQuery(id+"F2.boolean.opBoolean","SPLIT",FACE,{"disambiguationData":[TD([makeQuery(id+"F1.opExtrude","SWEPT_FACE",FACE,{"disambiguationData":[OSD([subQ6])]})])],"derivedFrom":makeQuery(id+"F1.opExtrude","CAP_FACE",FACE,{"disambiguationData":[OSD([subQ6,subQ8,subQ9,subQ7,subQ4,subQ3,subQ2,subQ1,subQ0,subQ5,subQ10,subQ11])],"isStart":true})});}
            var sketch = newSketch(context, id + "F16", { "sketchPlane" : qUnion([Q0])});
            skArc(sketch, "E79.0", {"start": v(-64.25, 74.25) * mm, "mid": v(-71.32, 71.32) * mm, "end": v(-74.25, 64.25) * mm});
            skLineSegment(sketch, "E79.1", {"start": v(-74.25, -64.25) * mm, "end": v(-74.25, 64.25) * mm});
            skLineSegment(sketch, "E79.2", {"start": v(-64.25, 74.25) * mm, "end": v(64.25, 74.25) * mm});
            skArc(sketch, "E79.3", {"start": v(74.25, 64.25) * mm, "mid": v(71.32, 71.32) * mm, "end": v(64.25, 74.25) * mm});
            skLineSegment(sketch, "E79.4", {"start": v(74.25, -64.25) * mm, "end": v(74.25, 64.25) * mm});
            skArc(sketch, "E79.5", {"start": v(64.25, -74.25) * mm, "mid": v(71.32, -71.32) * mm, "end": v(74.25, -64.25) * mm});
            skLineSegment(sketch, "E79.6", {"start": v(-64.25, -74.25) * mm, "end": v(64.25, -74.25) * mm});
            skArc(sketch, "E79.7", {"start": v(-74.25, -64.25) * mm, "mid": v(-71.32, -71.32) * mm, "end": v(-64.25, -74.25) * mm});
            skCircle(sketch, "E79.8", {"center": v(-60, -60) * mm, "radius": 4 * mm});
            skCircle(sketch, "E79.9", {"center": v(-60, 60) * mm, "radius": 4 * mm});
            skCircle(sketch, "E79.10", {"center": v(60, 60) * mm, "radius": 4 * mm});
            skCircle(sketch, "E79.11", {"center": v(60, -60) * mm, "radius": 4 * mm});
            skArc(sketch, "E79.12", {"start": v(54.26, 47.88) * mm, "mid": v(0, 60) * mm, "end": v(-54.26, 47.88) * mm});
            skArc(sketch, "E79.13", {"start": v(-54.26, 47.88) * mm, "mid": v(-58.44, 44.2) * mm, "end": v(-60, 38.83) * mm});
            skLineSegment(sketch, "E79.14", {"start": v(-60, 38.83) * mm, "end": v(-60, -38.83) * mm});
            skArc(sketch, "E79.15", {"start": v(-60, -38.83) * mm, "mid": v(-58.44, -44.2) * mm, "end": v(-54.26, -47.88) * mm});
            skArc(sketch, "E79.16", {"start": v(-54.26, -47.88) * mm, "mid": v(0, -60) * mm, "end": v(54.26, -47.88) * mm});
            skArc(sketch, "E79.17", {"start": v(54.26, -47.88) * mm, "mid": v(58.44, -44.2) * mm, "end": v(60, -38.83) * mm});
            skLineSegment(sketch, "E79.18", {"start": v(60, 38.83) * mm, "end": v(60, -38.83) * mm});
            skArc(sketch, "E79.19", {"start": v(60, 38.83) * mm, "mid": v(58.44, 44.2) * mm, "end": v(54.26, 47.88) * mm});
            skPoint(sketch, "E80.endSnap0", {"position": v(0, 74.25) * mm});
            skLineSegment(sketch, "E81", {"start": v(-15, 92.25) * mm, "end": v(-33, 74.25) * mm});
            skLineSegment(sketch, "E82", {"start": v(15, 104.25) * mm, "end": v(15, 92.25) * mm});
            skLineSegment(sketch, "E83", {"start": v(15, 92.25) * mm, "end": v(33, 74.25) * mm});
            skCircle(sketch, "E84", {"center": v(0, 104.25) * mm, "radius": 6 * mm});
            skArc(sketch, "E85", {"start": v(15, 104.25) * mm, "mid": v(0, 119.25) * mm, "end": v(-15, 104.25) * mm});
            skLineSegment(sketch, "E86", {"start": v(-15, 104.25) * mm, "end": v(-15, 92.25) * mm});
            skLineSegment(sketch, "E87", {"start": v(-74.25, 0) * mm, "end": v(74.25, 0) * mm, "construction": true});
            skArc(sketch, "E88.MirrorCS", {"start": v(-15, 104.25) * mm, "mid": v(0, 119.25) * mm, "end": v(15, 104.25) * mm});
            skLineSegment(sketch, "E89.MirrorCS", {"start": v(64.25, 74.25) * mm, "end": v(-64.25, 74.25) * mm});
            skLineSegment(sketch, "E90.MirrorCS", {"start": v(15, -92.25) * mm, "end": v(33, -74.25) * mm});
            skLineSegment(sketch, "E91.MirrorCS", {"start": v(-15, -92.25) * mm, "end": v(-33, -74.25) * mm});
            skLineSegment(sketch, "E92.MirrorCS", {"start": v(15, -104.25) * mm, "end": v(15, -92.25) * mm});
            skLineSegment(sketch, "E93.MirrorCS", {"start": v(-15, -104.25) * mm, "end": v(-15, -92.25) * mm});
            skLineSegment(sketch, "E94.MirrorCS", {"start": v(0, -74.25) * mm, "end": v(0, -104.25) * mm, "construction": true});
            skCircle(sketch, "E95.MirrorC", {"center": v(0, -104.25) * mm, "radius": 6 * mm});
            skArc(sketch, "E96.MirrorCS", {"start": v(15, -104.25) * mm, "mid": v(0, -119.25) * mm, "end": v(-15, -104.25) * mm});
            skSolve(sketch);
        }
        {
            var Q0;
            Q0 = qSketchRegion(id + "F16", true);
            var Q1;
            Q1=makeQuery(id+"F2.opExtrude","CAP_FACE",FACE,{"disambiguationData":[OSD([sQuery(id+"F0.wireOp",EDGE,"E12"),sQuery(id+"F0.wireOp",EDGE,"E13"),sQuery(id+"F0.wireOp",EDGE,"E14"),sQuery(id+"F0.wireOp",EDGE,"E15"),sQuery(id+"F0.wireOp",EDGE,"E17.filletArc"),sQuery(id+"F0.wireOp",EDGE,"E18.filletArc"),sQuery(id+"F0.wireOp",EDGE,"E19.filletArc"),sQuery(id+"F0.wireOp",EDGE,"E20.filletArc"),sQuery(id+"F0.wireOp",EDGE,"E25.0"),sQuery(id+"F0.wireOp",EDGE,"E25.1"),sQuery(id+"F0.wireOp",EDGE,"E25.2"),sQuery(id+"F0.wireOp",EDGE,"E25.3"),sQuery(id+"F0.wireOp",EDGE,"E25.4"),sQuery(id+"F0.wireOp",EDGE,"E25.5"),sQuery(id+"F0.wireOp",EDGE,"E25.6"),sQuery(id+"F0.wireOp",EDGE,"E25.7")])],"isStart":false});
            extrude(context, id + "F17", {"entities" : qUnion([Q0]), "endBound" : BoundingType.UP_TO_SURFACE, "endBoundEntityFace" : qUnion([Q1]), "depth" : 25 * mm});
        }
    });
